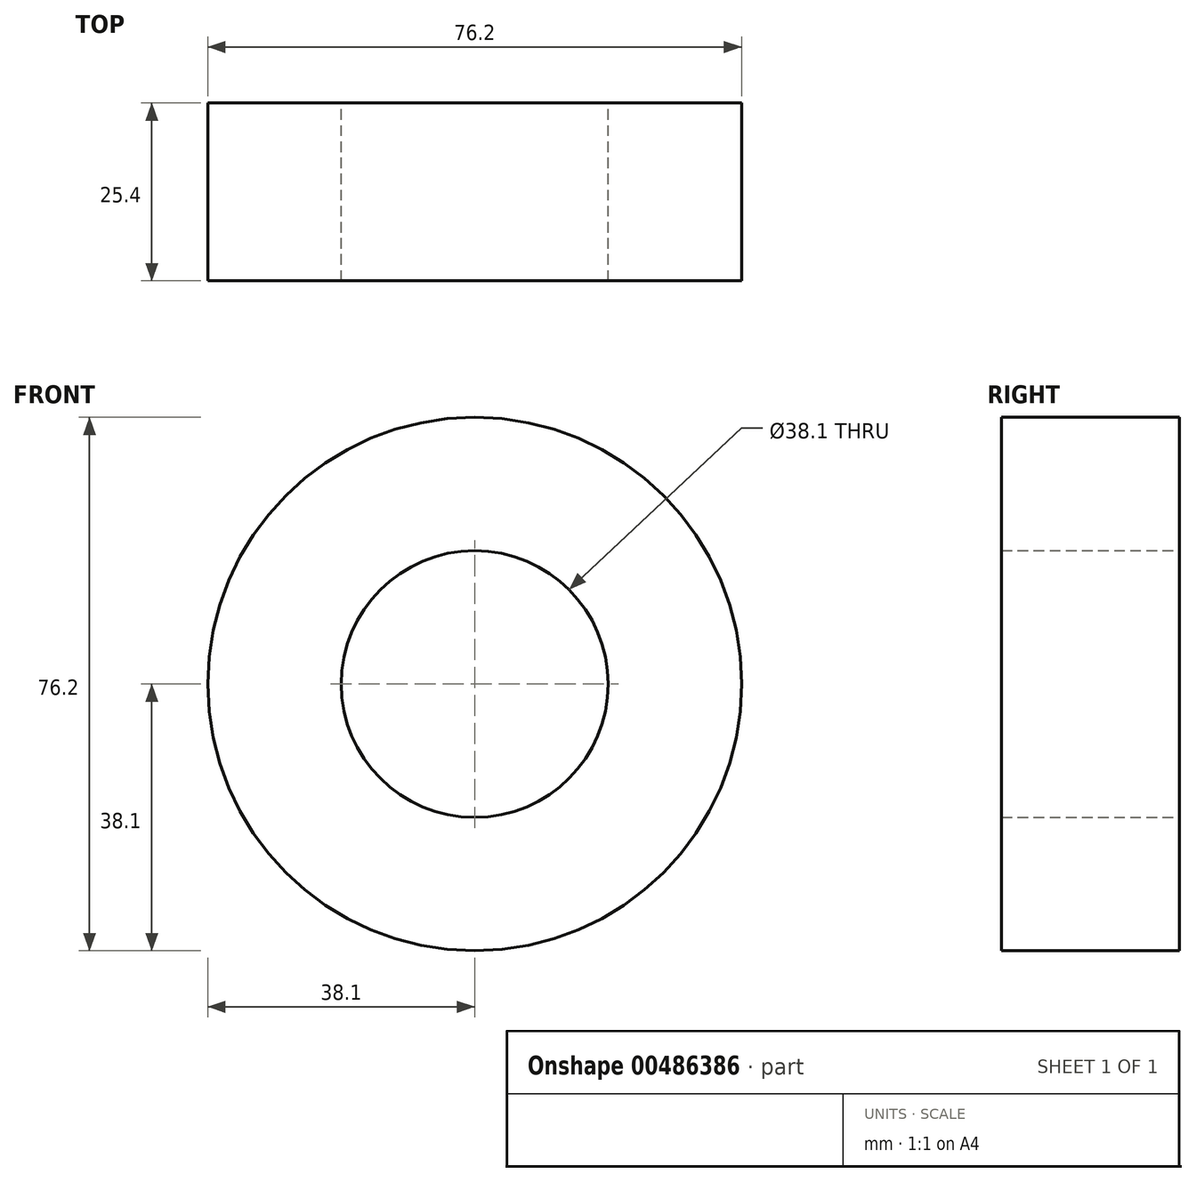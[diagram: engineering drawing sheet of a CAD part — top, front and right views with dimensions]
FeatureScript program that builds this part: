
annotation { "Feature Type Name" : "Feature", "Feature Type Description" : "" }
export const myFeature = defineFeature(function(context is Context, id is Id, definition is map)
    precondition{}
    {
        {
            var Q0;
            Q0=qCreatedBy(makeId("Front.planeOp"),FACE);
            var sketch = newSketch(context, id + "F0", { "sketchPlane" : qUnion([Q0])});
            skCircle(sketch, "E0", {"center": v(0, 0) * mm, "radius": 19.05 * mm});
            skCircle(sketch, "E1", {"center": v(0, 0) * mm, "radius": 38.1 * mm});
            skSolve(sketch);
        }
        {
            var Q0;
            Q0 = qSketchRegion(id + "F0", true);
            var sketch = newSketch(context, id + "F1", { "sketchPlane" : qUnion([Q0])});
            skSolve(sketch);
        }
        {
            var Q0;
            Q0 = qSketchRegion(id + "F1", true);
            var Q1;
            Q1=makeQuery(id+"F0.imprint","IMPRINT",FACE,{"disambiguationData":[TD([[makeQuery(id+"F0.imprint","IMPRINT",EDGE,{"derivedFrom":sQuery(id+"F0.wireOp",EDGE,"E0")}),-1.0]])]});
            extrude(context, id + "F2", {"entities" : qUnion([Q0, Q1]), "depth" : 25.4 * mm});
        }
    });
